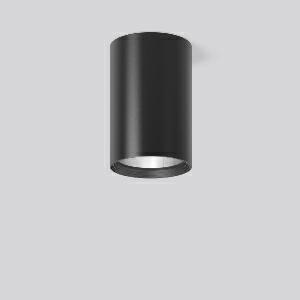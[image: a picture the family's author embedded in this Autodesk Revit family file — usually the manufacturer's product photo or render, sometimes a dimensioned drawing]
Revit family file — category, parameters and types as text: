
# Revit family: heledon_maxi_a_931217_003_2_76_6aa2
name_source: partatom
category: Lighting Fixtures
units: mm (PartAtom-declared; Revit-internal decimal feet)

## family parameters
Cut with Voids When Loaded = No
Host = Face
Light Source = No
Part Type = Normal
Room Calculation Point = No
Round Connector Dimension = Use Diameter
Shared = No

## types (1)
- HELEDON maxi A (1 x LED Modul 927, 3150 lm, 2700)
    Apparent Load = 25 VA
    Approval mark = CE
    CIE Flux Codes = 100 100 100 100 100
    Color Rendering = 92
    Color Temperature = 2700
    Default Elevation = 1800 mm
    Description = Series: HELEDON maxi
Cylindrical surface-mounted downlight. Housing: die-cast aluminium, powder-coated. Internal ceiling frame polycarbonate with bayonet mounting. Black plastic ring and recessed LED to prevent glare from the side. Optical assembly with reflector made of MIRO-Silver with 98% total light reflection for outstanding efficiency - can be changed without tools. Best colour rendering index Ra>90. Suitable for Ceiling mounting. Easy installation with a separate ceiling frame with bayonet mounting and plug connection. Driver integrated. Connected via plug-in connector. High quality converter without flickering and stroboscopic effect. The following accessories can be mounted without use of tools: interchangeable lenses, decorative glasses, honeycomb louvre, clear and frosted diffusers, white interchangeable plastic ring. 
Colour: deep black, matt (RAL 9005)
Diameter: 123 mm
Height: 183 mm
Lamp: LED
Socket: without socket
Colour temperature: 2700K
Colour rendering index (CRI): 92
System power: 25 W
Rated luminous flux: 3150 lm
Luminous efficiency: 126 lm/W
Control gear: Converter, dimmable, DALI
Protection class: I
Type of protection: IP 20
    Height = 183 mm
    Lamp = 1 x LED Modul 927
    Lamp Light Flux = 3150 lm
    Lamp count = 1
    Length = 123 mm
    Lifetime = 50000 h
    Luminous efficacy = 126 lm/W
    Manufacturer = RZB
    ModVariant = No
    Model = 931217.003.2.76
    Mounting Place = Ceiling
    Mounting Type = Surface mounted
    Number of Poles = 1
    OnlyDefault = Yes
    Power Factor = 1
    Product Name = HELEDON maxi A
    Product group = Surface mounted downlights
    ProductGroupID = 302
    Protection Class = Protection class I
    Protection Degree = IP 20
    RLX_Detail_Level = 1
    RLX_Emergency_Light_Flux = 0 lm
    RLX_Emergency_Type = 0
    RLX_Emergency_Type_DB = No
    RlxData = <blob elided: 96021 chars, md5=16ab5faa>
    Socket = socket
    Standby Power = 0 W
    System Light Flux = 3150 lm
    System Power = 25 W
    Type Comments = Product without accessories
    Type Image = 931192.003.jpg
    URL = http://relux.com
    VarID = ---
    Voltage = 230 V
    Voltage Range = 220-240 V
    Weight = 0.00 kg
    Width = 0 mm  [stored 0 ft]

note: [stored X ft] marks values corroborated as IEEE doubles in the binary element streams (Revit-internal decimal feet)

## geometry (parser evidence)
native form markers: Blend x4, Sweep x10
no freeform markers — native parametric forms only
